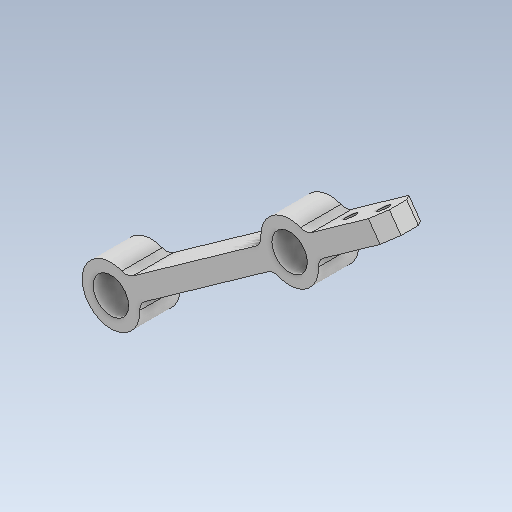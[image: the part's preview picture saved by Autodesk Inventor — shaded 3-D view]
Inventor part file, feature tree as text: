
AUTODESK INVENTOR PART (.ipt)
format: ipt  version: 2023 (Build 270158000, 158)  size: 157,696 bytes
history: native  units: mm
features: other x3, extrude x2, sketch x2, reference x2, fillet x1, chamfer x1, projected_geometry x1
ambient origin geometry x8: Origin, YZ Plane, XZ Plane, XY Plane, X Axis, Y Axis, Z Axis, Center Point
bodies: Solid1 (feature_tree)
feature tree (12):
  extrude  "Extrusion1"  Depth=10.0mm
  extrude  "Extrusion2"  Depth=2.0mm
  fillet  "Fillet1"  Radius=3.5mm
  chamfer  "Chamfer1"  Distance=20.0mm
  sketch  "Sketch1"  dims[d0=10.0mm d1=10.0mm]
  reference  "Reference1"
  reference  "Reference2"
  sketch  "Sketch2"  dims[d2=6.15mm d3=6.15mm d4=3.5mm d5=20.0mm d6=3.5mm d7=7.0mm d8=0.0mm d9=8.0mm d10=5.0mm d11=2.0mm d12=2.0mm d13=2.0mm d14=5.0mm d15=0.0mm d17=2.0mm d18=2.0mm d19=2.0mm d20=45.0deg]
  projected_geometry  "Projected Loop1"
  parser-record x1  (decoder bookkeeping rows leaked as tree rows — omitted from the tree; the rows remain in map.json)
  other  "leg_1.iam"
  other  "leg_holder_2:1"
note: 1 file-system path scrubbed to <path> (originals preserved in map.json)
